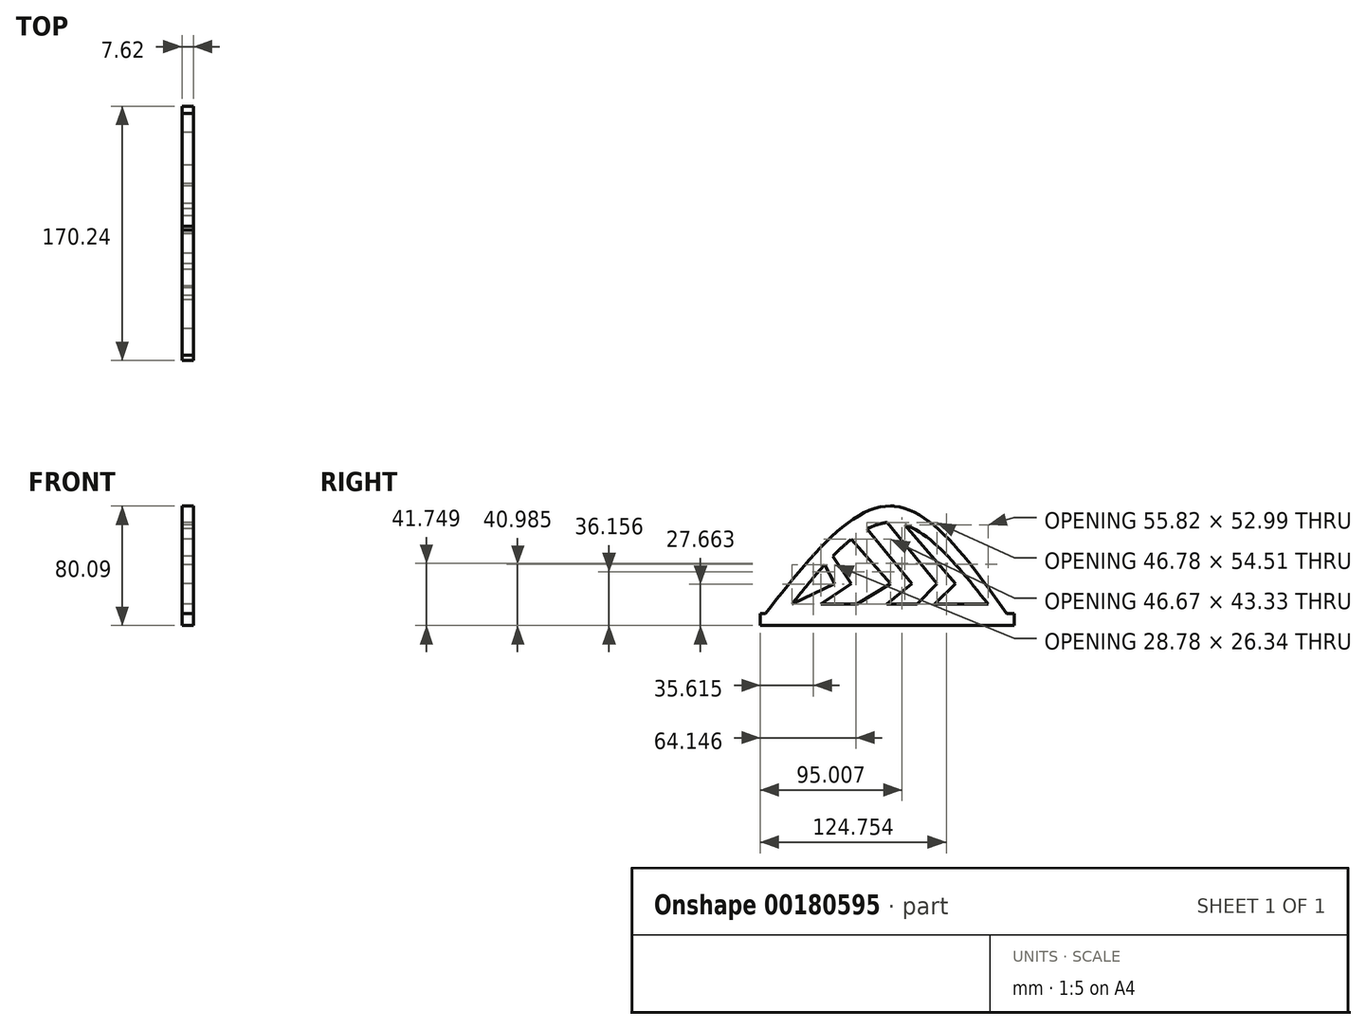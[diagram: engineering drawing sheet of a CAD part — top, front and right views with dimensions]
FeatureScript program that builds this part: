
annotation { "Feature Type Name" : "Feature", "Feature Type Description" : "" }
export const myFeature = defineFeature(function(context is Context, id is Id, definition is map)
    precondition{}
    {
        {
            var Q0;
            Q0=qCreatedBy(makeId("Right.planeOp"),FACE);
            var sketch = newSketch(context, id + "F0", { "sketchPlane" : qUnion([Q0])});
            skLineSegment(sketch, "E0", {"start": v(-76.04, 0) * mm, "end": v(72.84, 0) * mm});
            skLineSegment(sketch, "E1", {"start": v(-65.67, 0) * mm, "end": v(-56.62, 0) * mm});
            skLineSegment(sketch, "E2", {"start": v(-68.34, 0) * mm, "end": v(-65.67, 0) * mm});
            skLineSegment(sketch, "E3", {"start": v(-59.1, 0) * mm, "end": v(-56.62, 0) * mm});
            skLineSegment(sketch, "E4", {"start": v(-56.62, 0) * mm, "end": v(-50.11, 0) * mm});
            skLineSegment(sketch, "E5", {"start": v(-50.11, 0) * mm, "end": v(-47.21, 0) * mm});
            skLineSegment(sketch, "E6", {"start": v(-47.21, 0) * mm, "end": v(-40.96, 0) * mm});
            skLineSegment(sketch, "E7", {"start": v(-40.96, 0) * mm, "end": v(-38.06, 0) * mm});
            skLineSegment(sketch, "E8", {"start": v(-38.06, 0) * mm, "end": v(-31.65, 0) * mm});
            skLineSegment(sketch, "E9", {"start": v(-31.65, 0) * mm, "end": v(-28.9, 0) * mm});
            skLineSegment(sketch, "E10", {"start": v(-28.9, 0) * mm, "end": v(-22.5, 0) * mm});
            skLineSegment(sketch, "E11", {"start": v(-22.5, 0) * mm, "end": v(-19.9, 0) * mm});
            skLineSegment(sketch, "E12", {"start": v(-19.9, 0) * mm, "end": v(-13.45, 0) * mm});
            skLineSegment(sketch, "E13", {"start": v(-13.45, 0) * mm, "end": v(-10.75, 0) * mm});
            skLineSegment(sketch, "E14", {"start": v(-10.75, 0) * mm, "end": v(-4.2, 0) * mm});
            skLineSegment(sketch, "E15", {"start": v(-4.2, 0) * mm, "end": v(-1.6, 0) * mm});
            skLineSegment(sketch, "E16", {"start": v(-1.6, 0) * mm, "end": v(4.8, 0) * mm});
            skLineSegment(sketch, "E17", {"start": v(4.8, 0) * mm, "end": v(7.4, 0) * mm});
            skLineSegment(sketch, "E18", {"start": v(7.4, 0) * mm, "end": v(13.8, 0) * mm});
            skLineSegment(sketch, "E19", {"start": v(13.8, 0) * mm, "end": v(16.7, 0) * mm});
            skLineSegment(sketch, "E20", {"start": v(16.7, 0) * mm, "end": v(23.11, 0) * mm});
            skLineSegment(sketch, "E21", {"start": v(23.11, 0) * mm, "end": v(25.7, 0) * mm});
            skLineSegment(sketch, "E22", {"start": v(25.7, 0) * mm, "end": v(32.11, 0) * mm});
            skLineSegment(sketch, "E23", {"start": v(32.11, 0) * mm, "end": v(34.55, 0) * mm});
            skLineSegment(sketch, "E24", {"start": v(34.55, 0) * mm, "end": v(40.96, 0) * mm});
            skLineSegment(sketch, "E25", {"start": v(40.96, 0) * mm, "end": v(43.7, 0) * mm});
            skLineSegment(sketch, "E26", {"start": v(43.7, 0) * mm, "end": v(50.11, 0) * mm});
            skLineSegment(sketch, "E27", {"start": v(50.11, 0) * mm, "end": v(52.7, 0) * mm});
            skLineSegment(sketch, "E28", {"start": v(52.7, 0) * mm, "end": v(59.26, 0) * mm});
            skLineSegment(sketch, "E29", {"start": v(59.26, 0) * mm, "end": v(61.86, 0) * mm});
            skPoint(sketch, "E30.1.internal.orphan", {"position": v(0, 72.08) * mm});
            skPoint(sketch, "E30.startDerivative.orphan", {"position": v(-48.39, 36.22) * mm});
            skPoint(sketch, "E31.end.orphan", {"position": v(-47.21, 36.22) * mm});
            skLineSegment(sketch, "E32", {"start": v(-1.9, 72) * mm, "end": v(-1.86, 72.01) * mm});
            skFitSpline(sketch, "E33", {"points": [v(-66.26, 6.48) * mm, v(0, 72.08) * mm, v(65.18, 6.48) * mm], "startDerivative": vector(132.64, 196.65) * mm, "endDerivative": vector(130.23, -196.92) * mm});
            skLineSegment(sketch, "E34", {"start": v(-66.26, 6.48) * mm, "end": v(65.18, 6.48) * mm});
            skLineSegment(sketch, "E35", {"start": v(-76.04, 0) * mm, "end": v(-87.48, 0) * mm});
            skLineSegment(sketch, "E36", {"start": v(-87.48, 0) * mm, "end": v(-87.48, -8) * mm});
            skLineSegment(sketch, "E37", {"start": v(-87.48, -8) * mm, "end": v(82.76, -8) * mm});
            skLineSegment(sketch, "E38", {"start": v(82.76, -8) * mm, "end": v(82.76, 0) * mm});
            skLineSegment(sketch, "E39", {"start": v(82.76, 0) * mm, "end": v(72.84, 0) * mm});
            skLineSegment(sketch, "E40", {"start": v(-37.48, 19.96) * mm, "end": v(-66.26, 6.48) * mm});
            skLineSegment(sketch, "E41", {"start": v(-26.54, 19.96) * mm, "end": v(-46.67, 6.48) * mm});
            skLineSegment(sketch, "E42", {"start": v(0, 19.96) * mm, "end": v(-22.72, 6.48) * mm});
            skLineSegment(sketch, "E43", {"start": v(14.02, 19.96) * mm, "end": v(-2.58, 6.48) * mm});
            skLineSegment(sketch, "E44", {"start": v(30.92, 19.96) * mm, "end": v(17.74, 6.48) * mm});
            skLineSegment(sketch, "E45", {"start": v(43.26, 19.96) * mm, "end": v(29.45, 6.48) * mm});
            skFitSpline(sketch, "E46", {"points": [v(-83.9, 0) * mm, v(0, 72.08) * mm, v(77.8, 0) * mm], "startDerivative": vector(168.28, 215.5) * mm, "endDerivative": vector(155.07, -217.01) * mm});
            skFitSpline(sketch, "E47", {"points": [v(-66.26, 6.48) * mm, v(0, 61.1) * mm, v(65.18, 6.48) * mm], "startDerivative": vector(132.57, 163.7) * mm, "endDerivative": vector(130.3, -163.97) * mm});
            skLineSegment(sketch, "E48", {"start": v(-37.48, 19.96) * mm, "end": v(-44.1, 32.82) * mm});
            skLineSegment(sketch, "E49", {"start": v(-26.54, 19.96) * mm, "end": v(-38.87, 38.39) * mm});
            skLineSegment(sketch, "E50", {"start": v(0, 19.96) * mm, "end": v(-26.4, 49.81) * mm});
            skLineSegment(sketch, "E51", {"start": v(14.02, 19.96) * mm, "end": v(-15.86, 56.78) * mm});
            skLineSegment(sketch, "E52", {"start": v(30.92, 19.96) * mm, "end": v(-2.38, 61) * mm});
            skLineSegment(sketch, "E53", {"start": v(43.26, 19.96) * mm, "end": v(9.36, 59.47) * mm});
            skSolve(sketch);
        }
        {
            var Q0;
            Q0 = qSketchRegion(id + "F0", true);
            var Q1;
            {var subQ4=sQuery(id+"F0.wireOp",EDGE,"E40");Q1=makeQuery(id+"F0.imprint","IMPRINT",FACE,{"disambiguationData":[TD([[makeQuery(id+"F0.imprint","IMPRINT",EDGE,{"derivedFrom":subQ4}),1.0]])]});}
            var Q2;
            {var subQ1=sQuery(id+"F0.wireOp",EDGE,"E42");Q2=makeQuery(id+"F0.imprint","IMPRINT",FACE,{"disambiguationData":[TD([[makeQuery(id+"F0.imprint","IMPRINT",EDGE,{"derivedFrom":subQ1}),1.0]])]});}
            var Q3;
            {var subQ3=sQuery(id+"F0.wireOp",EDGE,"E44");Q3=makeQuery(id+"F0.imprint","IMPRINT",FACE,{"disambiguationData":[TD([[makeQuery(id+"F0.imprint","IMPRINT",EDGE,{"derivedFrom":subQ3}),1.0]])]});}
            extrude(context, id + "F1", {"entities" : qUnion([Q0, Q1, Q2, Q3]), "depth" : 7.62 * mm});
        }
    });
